# Revit family: rinnai_linear_fire_platform_1500
name_source: partatom
category: Specialty Equipment
units: mm (PartAtom-declared; Revit-internal decimal feet)

## family parameters
Always vertical = Yes
Cut with Voids When Loaded = No
Part Type = Normal
Room Calculation Point = No
Round Connector Dimension = Use Diameter
Shared = No
Work Plane-Based = No

## types (1)
- Fire Platform for Linear 1500 Series
    A = 50 mm  [stored 0.164042 ft]
    B = 400 mm  [stored 1.31234 ft]
    Depth = 335 mm  [stored 1.09908 ft]
    Fire Box Centre = 500 mm
    Fire Width = 1850 mm  [stored 6.06955 ft]
    Opening Width = 1950 mm  [stored 6.39764 ft]
    Thickness = 20 mm  [stored 0.0656168 ft]
    Type Comments = Plywood platform to support fire.
    m_platform = Rinnai Ply

note: [stored X ft] marks values corroborated as IEEE doubles in the binary element streams (Revit-internal decimal feet)

## geometry (parser evidence)
native form markers: Sweep x1
no freeform markers — native parametric forms only
